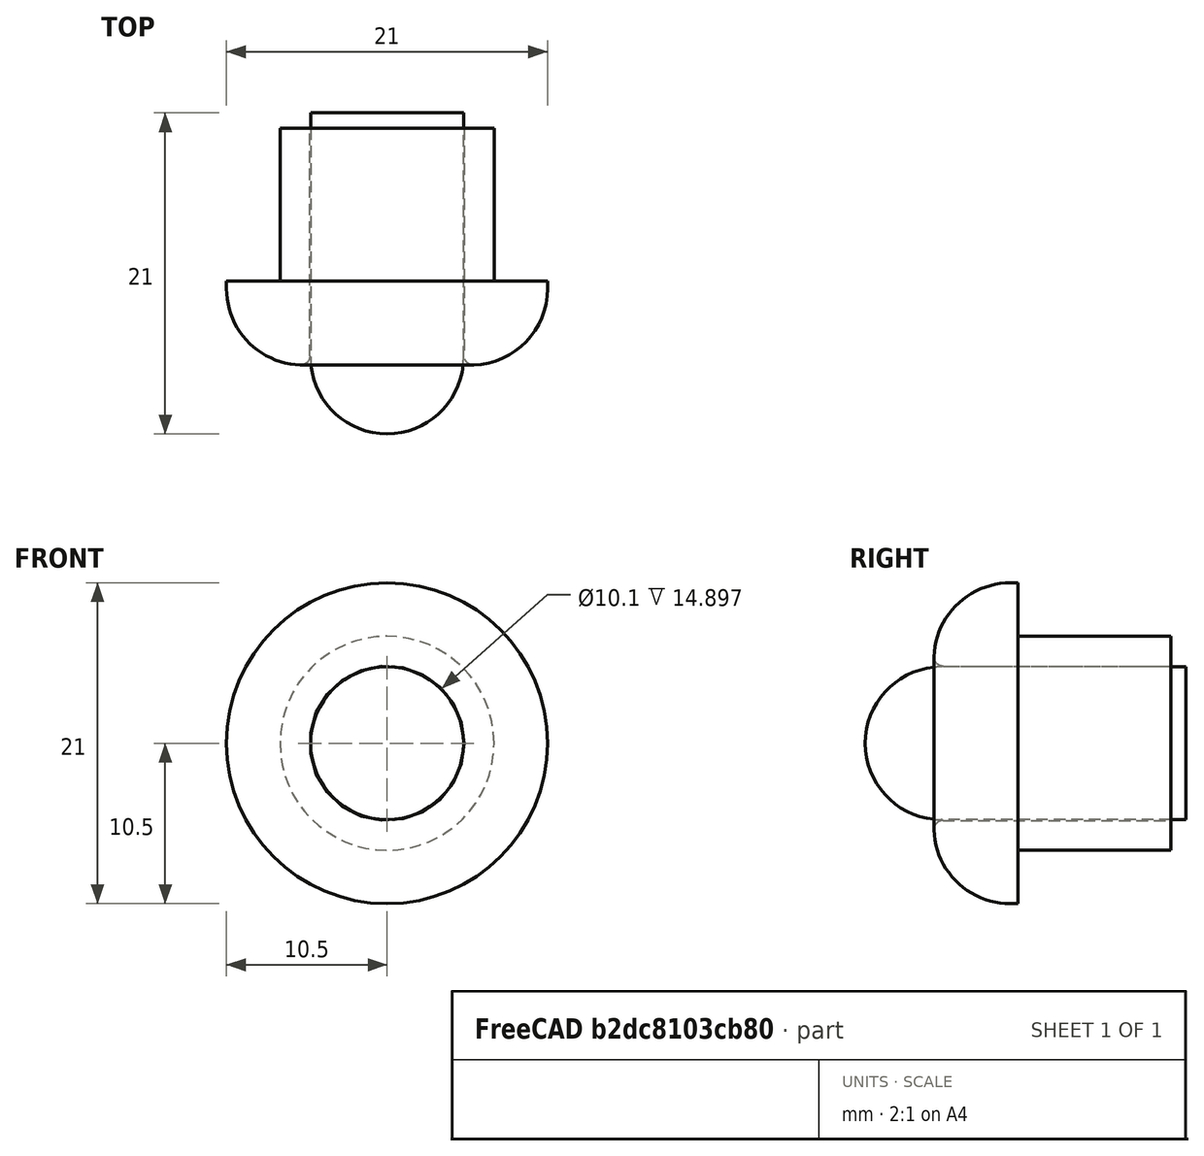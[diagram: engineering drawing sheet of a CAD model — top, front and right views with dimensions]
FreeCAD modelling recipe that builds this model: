
FCSTD DOCUMENT  (FreeCAD 0.19R)
Label: lamp
License: CreativeCommons Attribution-ShareAlike
LicenseURL: http://creativecommons.org/licenses/by-sa/4.0/
objects: PartDesign::SubShapeBinder×4, PartDesign::Pad×3, PartDesign::Fillet×2, PartDesign::Body×2, Part::Feature×2, PartDesign::Pocket×1, PartDesign::AdditiveSphere×1, App::Part×1
note: 20 computed .brp shape members not serialized (recipe doc carries the construction recipe); baked Part::Feature solids carry a one-line shape summary decoded from their .brp
EXTERNAL_REF file=base_dimensions.FCStd obj=Part
EXTERNAL_REF file=base_dimensions.FCStd obj=Spreadsheet
EXTERNAL_REF file=base_dimensions.FCStd obj=Sketch001

FEATURE [PartDesign::SubShapeBinder] Binder  label="Binder_lamp_outline_sketch"
  BindMode = 0
  ClaimChildren = false
  Context = -> Part [Body.Binder.]
  Fuse = false
  MakeFace = true
  PartialLoad = false
  Relative = true
  Support = -> [<external base_dimensions.FCStd>#Part[Body002.Sketch006.]]
  _Version = 1
FEATURE [PartDesign::Pad] Pad
  Length = 5.5
  Length2 = 100
  Profile = -> Binder [Face1]
  Reversed = true
  Type = 0
  expr: Length = <<base_dimensions>>#<<data>>.lamp_fillet_radius + 0.5mm
FEATURE [PartDesign::SubShapeBinder] Binder001  label="Binder_lamp_cutout_sketch"
  BindMode = 0
  ClaimChildren = false
  Context = -> Part [Body.Binder001.]
  Fuse = false
  MakeFace = true
  PartialLoad = false
  Relative = true
  Support = -> [<external base_dimensions.FCStd>#Part[Body002.Sketch007.]]
  _Version = 1
FEATURE [PartDesign::Pad] Pad001
  BaseFeature = -> Pad
  Length = 10
  Length2 = 100
  Profile = -> Binder001 [Face1]
  Type = 0
  expr: Length = <<base_dimensions>>#<<front_y>>.Constraints.thickness
FEATURE [PartDesign::SubShapeBinder] Binder002  label="Binder_lamp_cutout_in_sketch"
  BindMode = 0
  ClaimChildren = false
  Context = -> Part [Body.Binder002.]
  Fuse = false
  MakeFace = true
  PartialLoad = false
  Relative = true
  Support = -> [<external base_dimensions.FCStd>#Part[Body002.Sketch008.]]
  _Version = 1
FEATURE [PartDesign::Pocket] Pocket
  BaseFeature = -> Pad001
  Length = 5
  Length2 = 100
  Midplane = true
  Profile = -> Binder002 [Face1]
  Reversed = true
  Type = 1
FEATURE [PartDesign::Fillet] Fillet
  Base = -> Pocket [Edge3]
  BaseFeature = -> Pocket
  Radius = 5
  expr: Radius = <<base_dimensions>>#<<data>>.lamp_fillet_radius
FEATURE [PartDesign::SubShapeBinder] Binder003  label="Binder_lamp_base_sketch001"
  BindMode = 0
  ClaimChildren = false
  Context = -> Part [Body001.Binder003.]
  Fuse = false
  MakeFace = true
  PartialLoad = false
  Placement = pos=(0,-5,0) rot=(0,0,1;0rad)
  Relative = true
  Support = -> [<external base_dimensions.FCStd>#Part[Body002.Sketch005.]]
  _Version = 1
  expr: .Placement.Base.y = -5mm
FEATURE [PartDesign::Fillet] Fillet001
  Base = -> Fillet [Edge7]
  BaseFeature = -> Fillet
  Radius = 0.6
FEATURE [PartDesign::Body] Body  label="lamp_holder"
  Group = -> [Binder,Pad,Binder001,Pad001,Binder002,Pocket,Fillet,Fillet001]
  Origin = -> Origin001
  Tip = -> Fillet001
FEATURE [PartDesign::Pad] Pad002
  Length = 16
  Length2 = 100
  Placement = pos=(0,-5,0) rot=(0,0,1;0rad)
  Profile = -> Binder003 [Face1]
  Type = 0
FEATURE [PartDesign::AdditiveSphere] Sphere
  Angle1 = -90
  Angle2 = 90
  Angle3 = 180
  AttacherType = Attacher::AttachEngine3D
  AttachmentOffset = pos=(0,0,0) rot=(0,0,1;3.14159rad)
  BaseFeature = -> Pad002
  MapMode = 2
  Placement = pos=(0,-5,0) rot=(0,0,1;3.14159rad)
  Radius = 5
  Refine = true
  Support = -> [Binder003]
FEATURE [PartDesign::Body] Body001  label="lamp_glass"
  Group = -> [Binder003,Pad002,Sphere]
  Origin = -> Origin002
  Tip = -> Sphere
FEATURE [Part::Feature] Body__sc_export  label="lamp_holder__sc_export"
  shape: bbox 22.73 x 15.52 x 22.73 mm, 7 faces (baked)
FEATURE [Part::Feature] Body001__sc_export  label="lamp_glass__sc_export"
  shape: bbox 10 x 21 x 10 mm, 3 faces (baked)
FEATURE [App::Part] Part  label="lamp_part"
  Group = -> [Body,Body001,Body__sc_export,Body001__sc_export]
  Origin = -> Origin
